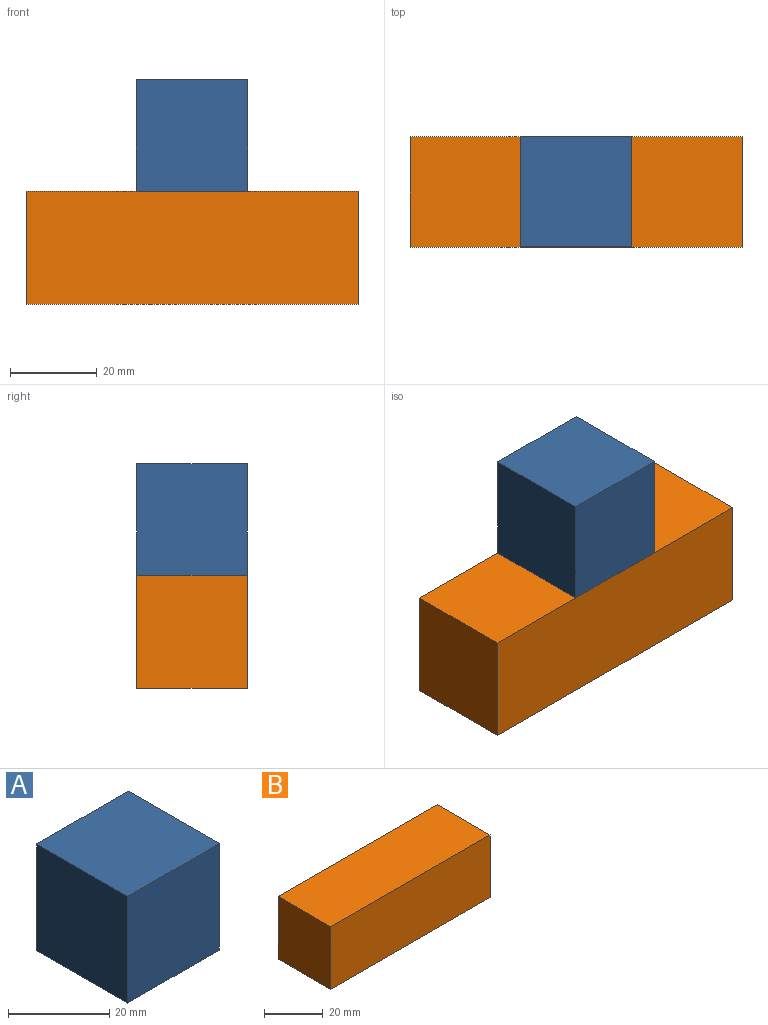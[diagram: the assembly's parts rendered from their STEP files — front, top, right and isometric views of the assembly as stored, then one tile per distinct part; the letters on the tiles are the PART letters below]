
ASSEMBLY  parts=2 mates=1
PART A: 6 faces, bbox 25.6x25.4x25.7 mm
  f0: plane 25.62x25.4mm, normal (0,0,1), area 650.6mm2, adj f1,f3,f4,f5
  f1: plane 25.73x25.4mm, normal (-1,0,0), area 653.7mm2, adj f0,f2,f4,f5
  f2: plane 25.62x25.4mm, normal (0,0,-1), area 650.6mm2, adj f1,f3,f4,f5
  f3: plane 25.73x25.4mm, normal (1,0,0), area 653.7mm2, adj f0,f2,f4,f5
  f4: plane 25.73x25.62mm, normal (0,-1,0), area 659.2mm2, adj f0,f1,f2,f3
  f5: plane 25.73x25.62mm, normal (0,1,0), area 659.2mm2, adj f0,f1,f2,f3
PART B: 6 faces, bbox 76.5x25.4x26.1 mm
  f0: plane 76.5x25.4mm, normal (0,0,1), area 1943.2mm2, adj f1,f3,f4,f5
  f1: plane 26.07x25.4mm, normal (-1,0,0), area 662.2mm2, adj f0,f2,f4,f5
  f2: plane 76.5x25.4mm, normal (0,0,-1), area 1943.2mm2, adj f1,f3,f4,f5
  f3: plane 26.07x25.4mm, normal (1,0,0), area 662.2mm2, adj f0,f2,f4,f5
  f4: plane 76.5x26.07mm, normal (0,-1,0), area 1994.6mm2, adj f0,f1,f2,f3
  f5: plane 76.5x26.07mm, normal (0,1,0), area 1994.6mm2, adj f0,f1,f2,f3
PLACE A t=(59.65,-21.87,15.39)mm
PLACE B t=(42.74,-21.87,17.74)mm
MATE fastened A.f2 <-> B.f0  axis (0,0,-1) through (-49.94,-34.57,4.44)mm
